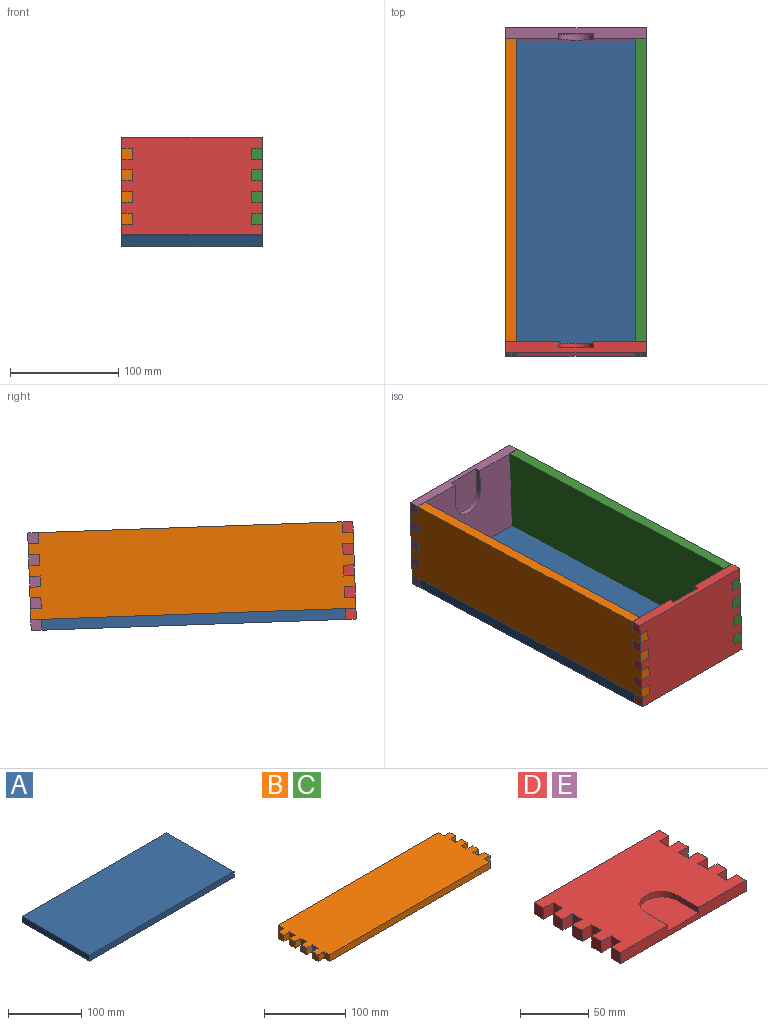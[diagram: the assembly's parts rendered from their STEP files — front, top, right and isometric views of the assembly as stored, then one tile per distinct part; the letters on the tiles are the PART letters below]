
ASSEMBLY  parts=5 mates=4
PART A: 6 faces, bbox 280x130x10 mm
  f0: plane 280x10mm, normal (0,-1,0), area 2800mm2, adj f1,f3,f4,f5
  f1: plane 130x10mm, normal (1,0,0), area 1300mm2, adj f0,f2,f4,f5
  f2: plane 280x10mm, normal (0,1,0), area 2800mm2, adj f1,f3,f4,f5
  f3: plane 130x10mm, normal (-1,0,0), area 1300mm2, adj f0,f2,f4,f5
  f4: plane 280x130mm, normal (0,0,1), area 36400mm2, adj f0,f1,f2,f3
  f5: plane 280x130mm, normal (0,0,-1), area 36400mm2, adj f0,f1,f2,f3
PART B: 38 faces, bbox 300x90x10 mm
  f0: plane 10x10mm, normal (1,0,0), area 100mm2, adj f1,f35,f36,f37
  f1: plane 10x10mm, normal (0,-1,0), area 100mm2, adj f0,f2,f36,f37
  f2: plane 10x10mm, normal (1,0,0), area 100mm2, adj f1,f3,f36,f37
  f3: plane 10x10mm, normal (0,1,0), area 100mm2, adj f2,f4,f36,f37
  f4: plane 10x10mm, normal (1,0,0), area 100mm2, adj f3,f5,f36,f37
  f5: plane 10x10mm, normal (0,-1,0), area 100mm2, adj f4,f6,f36,f37
  f6: plane 10x10mm, normal (1,0,0), area 100mm2, adj f5,f7,f36,f37
  f7: plane 10x10mm, normal (0,1,0), area 100mm2, adj f6,f8,f36,f37
  f8: plane 10x10mm, normal (1,0,0), area 100mm2, adj f7,f9,f36,f37
  f9: plane 10x10mm, normal (0,-1,0), area 100mm2, adj f8,f10,f36,f37
  f10: plane 10x10mm, normal (1,0,0), area 100mm2, adj f9,f11,f36,f37
  f11: plane 10x10mm, normal (0,1,0), area 100mm2, adj f10,f12,f36,f37
  f12: plane 10x10mm, normal (1,0,0), area 100mm2, adj f11,f13,f36,f37
  f13: plane 10x10mm, normal (0,-1,0), area 100mm2, adj f12,f14,f36,f37
  f14: plane 10x10mm, normal (1,0,0), area 100mm2, adj f13,f15,f36,f37
  f15: plane 10x10mm, normal (0,1,0), area 100mm2, adj f14,f16,f36,f37
  f16: plane 10x10mm, normal (1,0,0), area 100mm2, adj f15,f17,f36,f37
  f17: plane 280x10mm, normal (0,1,0), area 2800mm2, adj f16,f18,f36,f37
  f18: plane 10x10mm, normal (-1,0,0), area 100mm2, adj f17,f19,f36,f37
  f19: plane 10x10mm, normal (0,1,0), area 100mm2, adj f18,f20,f36,f37
  f20: plane 10x10mm, normal (-1,0,0), area 100mm2, adj f19,f21,f36,f37
  f21: plane 10x10mm, normal (0,-1,0), area 100mm2, adj f20,f22,f36,f37
  f22: plane 10x10mm, normal (-1,0,0), area 100mm2, adj f21,f23,f36,f37
  f23: plane 10x10mm, normal (0,1,0), area 100mm2, adj f22,f24,f36,f37
  f24: plane 10x10mm, normal (-1,0,0), area 100mm2, adj f23,f25,f36,f37
  f25: plane 10x10mm, normal (0,-1,0), area 100mm2, adj f24,f26,f36,f37
  f26: plane 10x10mm, normal (-1,0,0), area 100mm2, adj f25,f27,f36,f37
  f27: plane 10x10mm, normal (0,1,0), area 100mm2, adj f26,f28,f36,f37
  f28: plane 10x10mm, normal (-1,0,0), area 100mm2, adj f27,f29,f36,f37
  f29: plane 10x10mm, normal (0,-1,0), area 100mm2, adj f28,f30,f36,f37
  f30: plane 10x10mm, normal (-1,0,0), area 100mm2, adj f29,f31,f36,f37
  f31: plane 10x10mm, normal (0,1,0), area 100mm2, adj f30,f32,f36,f37
  f32: plane 10x10mm, normal (-1,0,0), area 100mm2, adj f31,f33,f36,f37
  f33: plane 10x10mm, normal (0,-1,0), area 100mm2, adj f32,f34,f36,f37
  f34: plane 10x10mm, normal (-1,0,0), area 100mm2, adj f33,f35,f36,f37
  f35: plane 280x10mm, normal (0,-1,0), area 2800mm2, adj f0,f34,f36,f37
  f36: plane 300x90mm, normal (0,0,1), area 26000mm2, adj f0,f1,f2,f3,f4,f5,f6,f7
  f37: plane 300x90mm, normal (0,0,-1), area 26000mm2, adj f0,f1,f2,f3,f4,f5,f6,f7
PART C: same geometry as B
PART D: 42 faces, bbox 130x90x10 mm
  f0: cylinder r=16mm len=32mm, axis (0,0,-1), area 251.3mm2, adj f1,f38,f39,f41
  f1: plane 22.5x5mm, normal (-1,0,0), area 112.5mm2, adj f0,f37,f39,f41
  f2: plane 10x10mm, normal (1,0,0), area 100mm2, adj f3,f37,f39,f40
  f3: plane 10x10mm, normal (0,1,0), area 100mm2, adj f2,f4,f39,f40
  f4: plane 10x10mm, normal (1,0,0), area 100mm2, adj f3,f5,f39,f40
  f5: plane 10x10mm, normal (0,-1,0), area 100mm2, adj f4,f6,f39,f40
  f6: plane 10x10mm, normal (1,0,0), area 100mm2, adj f5,f7,f39,f40
  f7: plane 10x10mm, normal (0,1,0), area 100mm2, adj f6,f8,f39,f40
  f8: plane 10x10mm, normal (1,0,0), area 100mm2, adj f7,f9,f39,f40
  f9: plane 10x10mm, normal (0,-1,0), area 100mm2, adj f8,f10,f39,f40
  f10: plane 10x10mm, normal (1,0,0), area 100mm2, adj f9,f11,f39,f40
  f11: plane 10x10mm, normal (0,1,0), area 100mm2, adj f10,f12,f39,f40
  f12: plane 10x10mm, normal (1,0,0), area 100mm2, adj f11,f13,f39,f40
  f13: plane 10x10mm, normal (0,-1,0), area 100mm2, adj f12,f14,f39,f40
  f14: plane 10x10mm, normal (1,0,0), area 100mm2, adj f13,f15,f39,f40
  f15: plane 10x10mm, normal (0,1,0), area 100mm2, adj f14,f16,f39,f40
  f16: plane 10x10mm, normal (1,0,0), area 100mm2, adj f15,f17,f39,f40
  f17: plane 10x10mm, normal (0,-1,0), area 100mm2, adj f16,f18,f39,f40
  f18: plane 10x10mm, normal (1,0,0), area 100mm2, adj f17,f19,f39,f40
  f19: plane 130x10mm, normal (0,1,0), area 1300mm2, adj f18,f20,f39,f40
  f20: plane 10x10mm, normal (-1,0,0), area 100mm2, adj f19,f21,f39,f40
  f21: plane 10x10mm, normal (0,-1,0), area 100mm2, adj f20,f22,f39,f40
  f22: plane 10x10mm, normal (-1,0,0), area 100mm2, adj f21,f23,f39,f40
  f23: plane 10x10mm, normal (0,1,0), area 100mm2, adj f22,f24,f39,f40
  f24: plane 10x10mm, normal (-1,0,0), area 100mm2, adj f23,f25,f39,f40
  f25: plane 10x10mm, normal (0,-1,0), area 100mm2, adj f24,f26,f39,f40
  f26: plane 10x10mm, normal (-1,0,0), area 100mm2, adj f25,f27,f39,f40
  f27: plane 10x10mm, normal (0,1,0), area 100mm2, adj f26,f28,f39,f40
  f28: plane 10x10mm, normal (-1,0,0), area 100mm2, adj f27,f29,f39,f40
  f29: plane 10x10mm, normal (0,-1,0), area 100mm2, adj f28,f30,f39,f40
  f30: plane 10x10mm, normal (-1,0,0), area 100mm2, adj f29,f31,f39,f40
  f31: plane 10x10mm, normal (0,1,0), area 100mm2, adj f30,f32,f39,f40
  f32: plane 10x10mm, normal (-1,0,0), area 100mm2, adj f31,f33,f39,f40
  f33: plane 10x10mm, normal (0,-1,0), area 100mm2, adj f32,f34,f39,f40
  f34: plane 10x10mm, normal (-1,0,0), area 100mm2, adj f33,f35,f39,f40
  f35: plane 10x10mm, normal (0,1,0), area 100mm2, adj f34,f36,f39,f40
  f36: plane 10x10mm, normal (-1,0,0), area 100mm2, adj f35,f37,f39,f40
  f37: plane 130x10mm, normal (0,-1,0), area 1140mm2, adj f1,f2,f36,f38,f39,f40,f41
  f38: plane 22.5x5mm, normal (1,0,0), area 112.5mm2, adj f0,f37,f39,f41
  f39: plane 130x90mm, normal (0,0,1), area 9777.9mm2, adj f0,f1,f2,f3,f4,f5,f6,f7
  f40: plane 130x90mm, normal (0,0,-1), area 10900mm2, adj f2,f3,f4,f5,f6,f7,f8,f9
  f41: plane 38.5x32mm, normal (0,0,1), area 1122.1mm2, adj f0,f1,f37,f38
PART E: same geometry as D
PLACE A rot(axis=(-0.02,0.02,1),90deg) t=(-72.25,-15.62,80.01)mm
PLACE B rot(axis=(0.57,-0.59,-0.57),118.8deg) t=(-127.25,-14.02,124.98)mm
PLACE C rot(axis=(0.57,0.59,0.57),118.8deg) t=(-17.25,-14.02,124.98)mm
PLACE D rot(axis=(-1,0,0),92deg) t=(-72.25,-163.93,130.32)mm
PLACE E rot(axis=(0,0.69,-0.72),180deg) t=(-72.25,135.88,119.65)mm
MATE fastened A.f3 <-> D.f39  axis (0,-1,0.04) through (-72.25,-155.53,84.99)mm
MATE fastened D.f35 <-> B.f15  axis (0,-0.04,-1) through (-132.25,-157.69,165.12)mm
MATE fastened D.f5 <-> C.f21  axis (0,0.04,1) through (-12.25,-158.04,155.12)mm
MATE fastened B.f19 <-> E.f3  axis (0,0.04,1) through (-132.25,132.13,154.81)mm
